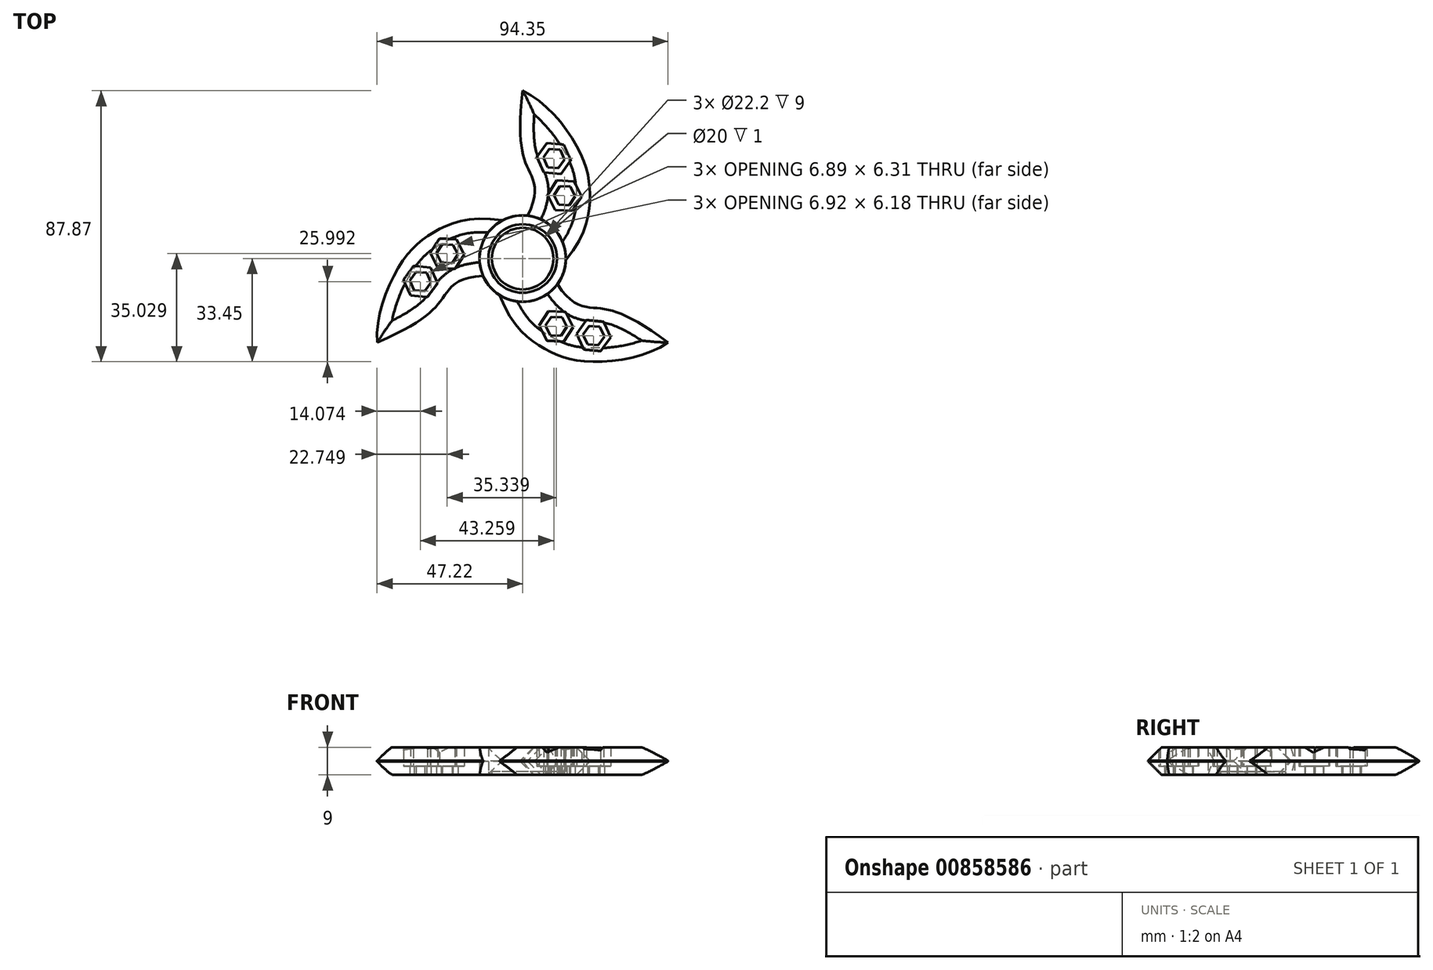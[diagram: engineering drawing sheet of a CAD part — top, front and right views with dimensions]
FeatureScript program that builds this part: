
annotation { "Feature Type Name" : "Feature", "Feature Type Description" : "" }
export const myFeature = defineFeature(function(context is Context, id is Id, definition is map)
    precondition{}
    {
        {
            var Q0;
            Q0=qCreatedBy(makeId("Top.planeOp"),FACE);
            var sketch = newSketch(context, id + "F0", { "sketchPlane" : qUnion([Q0])});
            skCircle(sketch, "E0", {"center": v(0, 0) * mm, "radius": 11.1 * mm});
            skLineSegment(sketch, "E1", {"start": v(0, 0) * mm, "end": v(0, 54.42) * mm, "construction": true});
            skLineSegment(sketch, "E2", {"start": v(0, 0) * mm, "end": v(63.41, -36.61) * mm, "construction": true});
            skFitSpline(sketch, "E3", {"points": [v(9.61, -5.55) * mm, v(21.8, 19.93) * mm, v(18.7, 34.28) * mm, v(0, 54.42) * mm], "startDerivative": vector(88.26, 91.6) * mm, "endDerivative": vector(-66.47, 31.25) * mm});
            skFitSpline(sketch, "E4", {"points": [v(0, 11.1) * mm, v(1.94, 28.71) * mm, v(0, 54.42) * mm], "startDerivative": vector(40.13, 65.5) * mm, "endDerivative": vector(10, 88.04) * mm});
            skCircle(sketch, "E5", {"center": v(0, 0) * mm, "radius": 14 * mm});
            skCircle(sketch, "E6.cCircle", {"center": v(10.11, 32.43) * mm, "radius": 4.8 * mm, "construction": true});
            skLineSegment(sketch, "E6.0", {"start": v(13.35, 36.94) * mm, "end": v(15.63, 31.89) * mm});
            skLineSegment(sketch, "E6.1", {"start": v(15.63, 31.89) * mm, "end": v(12.4, 27.38) * mm});
            skLineSegment(sketch, "E6.2", {"start": v(12.4, 27.38) * mm, "end": v(6.88, 27.93) * mm});
            skLineSegment(sketch, "E6.3", {"start": v(6.88, 27.93) * mm, "end": v(4.6, 32.98) * mm});
            skLineSegment(sketch, "E6.4", {"start": v(4.6, 32.98) * mm, "end": v(7.83, 37.48) * mm});
            skLineSegment(sketch, "E6.5", {"start": v(7.83, 37.48) * mm, "end": v(13.35, 36.94) * mm});
            skPoint(sketch, "E6.0.midPoint", {"position": v(14.49, 34.41) * mm});
            skCircle(sketch, "E7", {"center": v(0, 0) * mm, "radius": 10 * mm});
            skCircle(sketch, "E8.cCircle", {"center": v(10.11, 32.43) * mm, "radius": 3 * mm, "construction": true});
            skLineSegment(sketch, "E8.0", {"start": v(13.56, 32.1) * mm, "end": v(11.54, 29.28) * mm});
            skLineSegment(sketch, "E8.1", {"start": v(11.54, 29.28) * mm, "end": v(8.1, 29.62) * mm});
            skLineSegment(sketch, "E8.2", {"start": v(8.1, 29.62) * mm, "end": v(6.67, 32.78) * mm});
            skLineSegment(sketch, "E8.3", {"start": v(6.67, 32.78) * mm, "end": v(8.69, 35.6) * mm});
            skLineSegment(sketch, "E8.4", {"start": v(8.69, 35.6) * mm, "end": v(12.13, 35.25) * mm});
            skLineSegment(sketch, "E8.5", {"start": v(12.13, 35.25) * mm, "end": v(13.56, 32.1) * mm});
            skPoint(sketch, "E8.0.midPoint", {"position": v(12.55, 30.68) * mm});
            skLineSegment(sketch, "E9", {"start": v(0, 0) * mm, "end": v(68.43, 0) * mm, "construction": true});
            skCircle(sketch, "E10.cCircle", {"center": v(13.6, 20.4) * mm, "radius": 4.8 * mm, "construction": true});
            skLineSegment(sketch, "E10.0", {"start": v(16.63, 25.04) * mm, "end": v(19.14, 20.1) * mm});
            skLineSegment(sketch, "E10.1", {"start": v(19.14, 20.1) * mm, "end": v(16.1, 15.46) * mm});
            skLineSegment(sketch, "E10.2", {"start": v(16.1, 15.46) * mm, "end": v(10.57, 15.76) * mm});
            skLineSegment(sketch, "E10.3", {"start": v(10.57, 15.76) * mm, "end": v(8.07, 20.7) * mm});
            skLineSegment(sketch, "E10.4", {"start": v(8.07, 20.7) * mm, "end": v(11.1, 25.35) * mm});
            skLineSegment(sketch, "E10.5", {"start": v(11.1, 25.35) * mm, "end": v(16.63, 25.04) * mm});
            skPoint(sketch, "E10.0.midPoint", {"position": v(17.88, 22.57) * mm});
            skCircle(sketch, "E11.cCircle", {"center": v(13.6, 20.4) * mm, "radius": 3 * mm, "construction": true});
            skLineSegment(sketch, "E11.0", {"start": v(15.17, 17.31) * mm, "end": v(11.7, 17.5) * mm});
            skLineSegment(sketch, "E11.1", {"start": v(11.7, 17.5) * mm, "end": v(10.14, 20.6) * mm});
            skLineSegment(sketch, "E11.2", {"start": v(10.14, 20.6) * mm, "end": v(12.04, 23.5) * mm});
            skLineSegment(sketch, "E11.3", {"start": v(12.04, 23.5) * mm, "end": v(15.5, 23.3) * mm});
            skLineSegment(sketch, "E11.4", {"start": v(15.5, 23.3) * mm, "end": v(17.06, 20.21) * mm});
            skLineSegment(sketch, "E11.5", {"start": v(17.06, 20.21) * mm, "end": v(15.17, 17.31) * mm});
            skPoint(sketch, "E11.0.midPoint", {"position": v(13.44, 17.4) * mm});
            skLineSegment(sketch, "E12", {"start": v(4.6, 32.98) * mm, "end": v(15.63, 31.89) * mm, "construction": true});
            skLineSegment(sketch, "E13", {"start": v(8.07, 20.7) * mm, "end": v(19.14, 20.1) * mm, "construction": true});
            skSolve(sketch);
        }
        {
            var Q0;
            Q0=qSketchRegion(id+"F0",true);
            extrude(context, id + "F1", {"entities" : qUnion([Q0]), "depth" : 9 * mm, "offsetDistance" : 25 * mm});
        }
        {
            var Q0;
            {var subQ0=sQuery(id+"F0.wireOp",EDGE,"E0");var subQ1=makeQuery(id+"F0.imprint","INTERSECT",VERTEX,{"derivedFrom":[subQ0,sQuery(id+"F0.wireOp",EDGE,"E3")]});Q0=makeQuery(id+"F0.imprint","IMPRINT",FACE,{"disambiguationData":[TD([[makeQuery(id+"F0.imprint","IMPRINT",EDGE,{"disambiguationData":[TD([[subQ1,1.0]])],"derivedFrom":subQ0}),1.0]])]});}
            extrude(context, id + "F2", {"entities" : qUnion([Q0]), "depth" : 1 * mm, "offsetDistance" : 25 * mm});
        }
        {
            var Q0;
            Q0=makeQuery(id+"F0.imprint","IMPRINT",FACE,{"disambiguationData":[TD([[makeQuery(id+"F0.imprint","IMPRINT",EDGE,{"derivedFrom":sQuery(id+"F0.wireOp",EDGE,"E6.0")}),-1.0]])]});
            var Q1;
            Q1=makeQuery(id+"F0.imprint","IMPRINT",FACE,{"disambiguationData":[TD([[makeQuery(id+"F0.imprint","IMPRINT",EDGE,{"derivedFrom":sQuery(id+"F0.wireOp",EDGE,"e9405604-b3fd-474f-b84a-674374f038b5.0.1.0")}),-1.0]])]});
            var Q2;
            Q2=makeQuery(id+"F0.imprint","IMPRINT",FACE,{"disambiguationData":[TD([[makeQuery(id+"F0.imprint","IMPRINT",EDGE,{"derivedFrom":sQuery(id+"F0.wireOp",EDGE,"E10.0")}),-1.0]])]});
            extrude(context, id + "F3", {"entities" : qUnion([Q0, Q1, Q2]), "operationType" : NewBodyOperationType.ADD, "depth" : 2.85 * mm, "offsetDistance" : 25 * mm});
        }
        {
            var Q0;
            Q0=qCreatedBy(makeId("Front.planeOp"),FACE);
            var sketch = newSketch(context, id + "F4", { "sketchPlane" : qUnion([Q0])});
            skLineSegment(sketch, "E14", {"start": v(0, 0) * mm, "end": v(0, 39.09) * mm, "construction": true});
            skSolve(sketch);
        }
        {
            var Q0;
            Q0=makeQuery(id+"F1.opExtrude","CAP_EDGE",EDGE,{"disambiguationData":[OSD([sQuery(id+"F0.wireOp",EDGE,"E4")])],"isStart":true});
            var Q1;
            Q1=makeQuery(id+"F1.opExtrude","CAP_EDGE",EDGE,{"disambiguationData":[OSD([sQuery(id+"F0.wireOp",EDGE,"E3")])],"isStart":true});
            var Q2;
            Q2=makeQuery(id+"F1.opExtrude","CAP_EDGE",EDGE,{"disambiguationData":[OSD([sQuery(id+"F0.wireOp",EDGE,"E4")])],"isStart":false});
            var Q3;
            Q3=makeQuery(id+"F1.opExtrude","CAP_EDGE",EDGE,{"disambiguationData":[OSD([sQuery(id+"F0.wireOp",EDGE,"E3")])],"isStart":false});
            chamfer(context, id + "F5", {"entities" : qUnion([Q0, Q1, Q2, Q3]), "width" : 4.4 * mm, "tangentPropagation" : true});
        }
        {
            var Q0;
            Q0=makeQuery(id+"F1.opExtrude","SWEPT_BODY",BODY,{"disambiguationData":[OSD([sQuery(id+"F0.wireOp",EDGE,"E0"),sQuery(id+"F0.wireOp",EDGE,"E3"),sQuery(id+"F0.wireOp",EDGE,"E4"),sQuery(id+"F0.wireOp",EDGE,"E5"),sQuery(id+"F0.wireOp",EDGE,"E6.0"),sQuery(id+"F0.wireOp",EDGE,"E6.1"),sQuery(id+"F0.wireOp",EDGE,"E6.2"),sQuery(id+"F0.wireOp",EDGE,"E6.3"),sQuery(id+"F0.wireOp",EDGE,"E6.4"),sQuery(id+"F0.wireOp",EDGE,"E6.5"),sQuery(id+"F0.wireOp",EDGE,"e9405604-b3fd-474f-b84a-674374f038b5.0.1.0"),sQuery(id+"F0.wireOp",EDGE,"e9405604-b3fd-474f-b84a-674374f038b5.0.1.1"),sQuery(id+"F0.wireOp",EDGE,"e9405604-b3fd-474f-b84a-674374f038b5.0.1.2"),sQuery(id+"F0.wireOp",EDGE,"e9405604-b3fd-474f-b84a-674374f038b5.0.1.3"),sQuery(id+"F0.wireOp",EDGE,"e9405604-b3fd-474f-b84a-674374f038b5.0.1.4"),sQuery(id+"F0.wireOp",EDGE,"e9405604-b3fd-474f-b84a-674374f038b5.0.1.5")])]});
            var Q1;
            Q1=sQuery(id+"F4.wireOp",EDGE,"E14");
            circularPattern(context, id + "F6", {"entities" : qUnion([Q0]), "axis" : qUnion([Q1]), "angle" : 360 * degree, "instanceCount" : 3, "equalSpace" : true});
        }
    });
